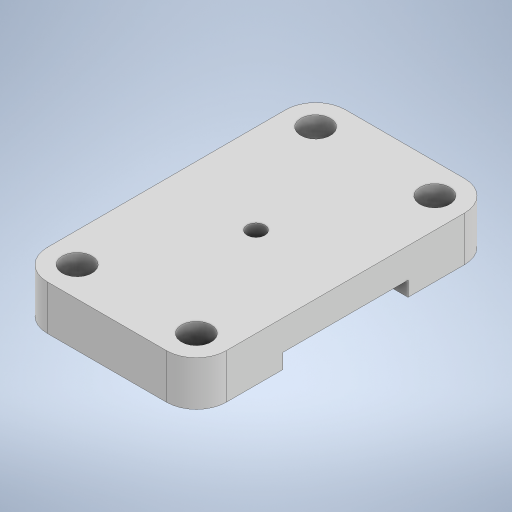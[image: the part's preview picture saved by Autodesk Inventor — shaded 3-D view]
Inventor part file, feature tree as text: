
AUTODESK INVENTOR PART (.ipt)
format: ipt  version: 2023.2 (Build 272271030, 271C)  size: 256,000 bytes
history: native  units: mm
features: extrude x2, sketch x2, fillet x1, projected_geometry x1
ambient origin geometry x8: Origin, YZ Plane, XZ Plane, XY Plane, X Axis, Y Axis, Z Axis, Center Point
bodies: Solid1 (feature_tree)
feature tree (6):
  extrude  "Extrusion1"  Depth=100.0mm
  fillet  "Fillet1"  Radius=10.0mm
  extrude  "Extrusion2"  Depth=5.0mm
  sketch  "Sketch1"  dims[d0=60.0mm d1=100.0mm d2=10.0mm]
  sketch  "Sketch2"  dims[d3=40.0mm d4=80.0mm d5=15.0mm d6=0.0mm d7=10.0mm d9=42.0mm d10=5.0mm d11=0.0mm d12=0.0mm d13=6.0mm]
  projected_geometry  "Projected Loop1"
